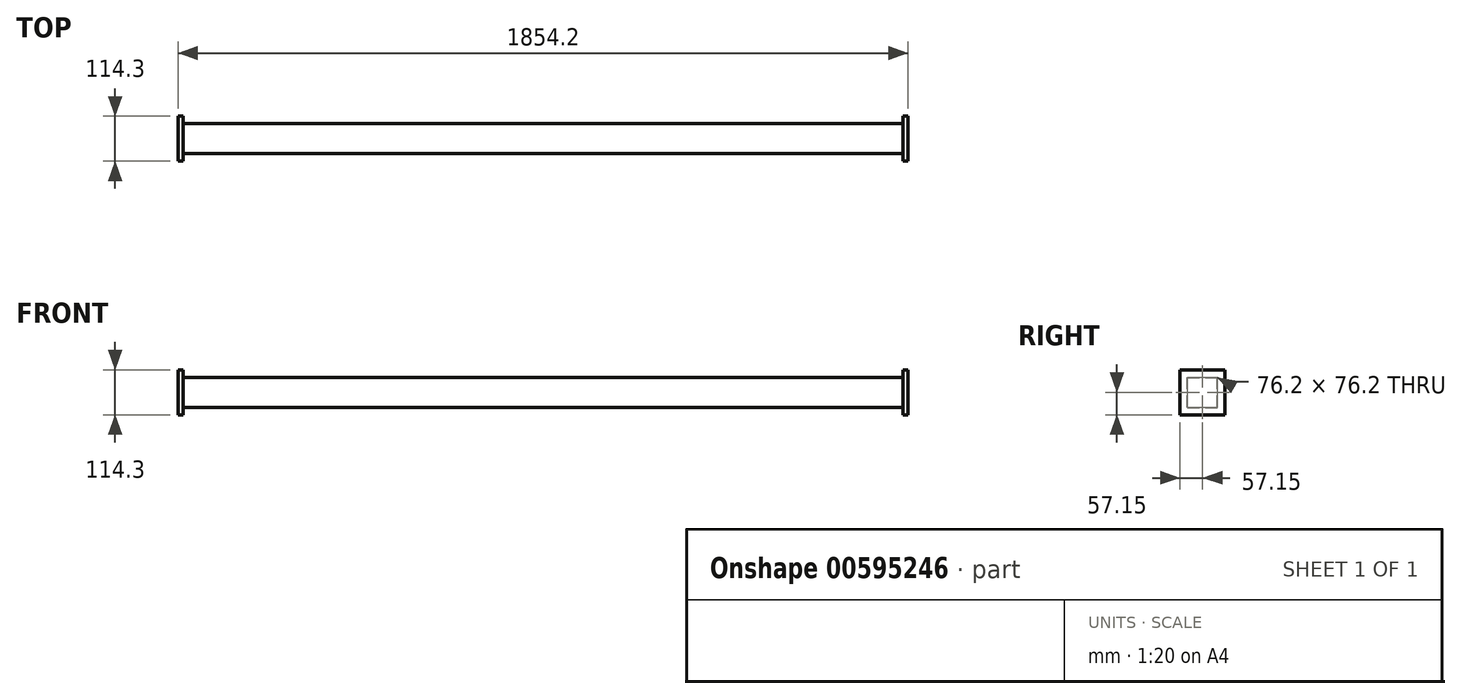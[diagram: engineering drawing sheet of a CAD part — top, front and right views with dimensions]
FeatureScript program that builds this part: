
annotation { "Feature Type Name" : "Feature", "Feature Type Description" : "" }
export const myFeature = defineFeature(function(context is Context, id is Id, definition is map)
    precondition{}
    {
        {
            var Q0;
            Q0=qCreatedBy(makeId("Right.planeOp"),FACE);
            var sketch = newSketch(context, id + "F0", { "sketchPlane" : qUnion([Q0])});
            skLineSegment(sketch, "E0.bottom", {"start": v(4231.19, -3979.39) * mm, "end": v(4078.79, -3979.39) * mm});
            skLineSegment(sketch, "E0.top", {"start": v(4231.19, -3826.99) * mm, "end": v(4078.79, -3826.99) * mm});
            skLineSegment(sketch, "E0.left", {"start": v(4231.19, -3979.39) * mm, "end": v(4231.19, -3826.99) * mm});
            skLineSegment(sketch, "E0.right", {"start": v(4078.79, -3979.39) * mm, "end": v(4078.79, -3826.99) * mm});
            skPoint(sketch, "E0.middle", {"position": v(4154.99, -3903.19) * mm});
            skSolve(sketch);
        }
        {
            var Q0;
            Q0=makeQuery(id+"F0.imprint","IMPRINT",FACE,{"disambiguationData":[TD([[makeQuery(id+"F0.imprint","IMPRINT",EDGE,{"derivedFrom":sQuery(id+"F0.wireOp",EDGE,"E0.bottom")}),-1.0]])]});
            extrude(context, id + "F1", {"entities" : qUnion([Q0]), "depth" : 12.7 * mm, "offsetDistance" : 25.4 * mm});
        }
        {
            var Q0;
            Q0=makeQuery(id+"F1.opExtrude","SWEPT_BODY",BODY,{"disambiguationData":[OSD([sQuery(id+"F0.wireOp",EDGE,"E0.bottom"),sQuery(id+"F0.wireOp",EDGE,"E0.top"),sQuery(id+"F0.wireOp",EDGE,"E0.left"),sQuery(id+"F0.wireOp",EDGE,"E0.right")])]});
            transform(context, id + "F2", {"entities" : qUnion([Q0]), "transformType" : TransformType.TRANSLATION_3D, "dx" : 706.12 * mm, "dy" : -1079.5 * mm, "dz" : 1186.18 * mm, "makeCopy" : false});
        }
        {
            var Q0;
            Q0=makeQuery(id+"F1.opExtrude","SWEPT_BODY",BODY,{"disambiguationData":[OSD([sQuery(id+"F0.wireOp",EDGE,"E0.bottom"),sQuery(id+"F0.wireOp",EDGE,"E0.top"),sQuery(id+"F0.wireOp",EDGE,"E0.left"),sQuery(id+"F0.wireOp",EDGE,"E0.right")])]});
            deleteBodies(context, id + "F3", {"entities" : qUnion([Q0])});
        }
        {
            var Q0;
            Q0=qCreatedBy(makeId("Front.planeOp"),FACE);
            var sketch = newSketch(context, id + "F4", { "sketchPlane" : qUnion([Q0])});
            skLineSegment(sketch, "E1.bottom", {"start": v(914.4, -38.1) * mm, "end": v(-914.4, -38.1) * mm});
            skLineSegment(sketch, "E1.top", {"start": v(914.4, 38.1) * mm, "end": v(-914.4, 38.1) * mm});
            skLineSegment(sketch, "E1.left", {"start": v(914.4, -38.1) * mm, "end": v(914.4, 38.1) * mm});
            skLineSegment(sketch, "E1.right", {"start": v(-914.4, -38.1) * mm, "end": v(-914.4, 38.1) * mm});
            skPoint(sketch, "E1.middle", {"position": v(0, 0) * mm});
            skSolve(sketch);
        }
        {
            var Q0;
            Q0=makeQuery(id+"F4.imprint","IMPRINT",FACE,{"disambiguationData":[TD([[makeQuery(id+"F4.imprint","IMPRINT",EDGE,{"derivedFrom":sQuery(id+"F4.wireOp",EDGE,"E1.bottom")}),-1.0]])]});
            extrude(context, id + "F5", {"entities" : qUnion([Q0]), "depth" : 76.2 * mm, "offsetDistance" : 25.4 * mm});
        }
        {
            var Q0;
            Q0=makeQuery(id+"F5.opExtrude","SWEPT_FACE",FACE,{"disambiguationData":[OSD([sQuery(id+"F4.wireOp",EDGE,"E1.left")])]});
            var sketch = newSketch(context, id + "F6", { "sketchPlane" : qUnion([Q0])});
            skLineSegment(sketch, "E2.bottom", {"start": v(19.05, -57.15) * mm, "end": v(-95.25, -57.15) * mm});
            skLineSegment(sketch, "E2.top", {"start": v(19.05, 57.15) * mm, "end": v(-95.25, 57.15) * mm});
            skLineSegment(sketch, "E2.left", {"start": v(19.05, -57.15) * mm, "end": v(19.05, 57.15) * mm});
            skLineSegment(sketch, "E2.right", {"start": v(-95.25, -57.15) * mm, "end": v(-95.25, 57.15) * mm});
            skPoint(sketch, "E2.middle", {"position": v(-38.1, 0) * mm});
            skPoint(sketch, "E2.middle.positionSnap0", {"position": v(-38.1, 38.1) * mm});
            skPoint(sketch, "E2.centerSnap0", {"position": v(-38.1, 38.1) * mm});
            skSolve(sketch);
        }
        {
            var Q0;
            {var subQ0=sQuery(id+"F4.wireOp",EDGE,"E1.left");Q0=makeQuery(id+"F6.imprint","IMPRINT",FACE,{"disambiguationData":[TD([[makeQuery(id+"F6.imprint","IMPRINT",EDGE,{"derivedFrom":makeQuery(id+"F5.opExtrude","CAP_EDGE",EDGE,{"disambiguationData":[OSD([subQ0])],"isStart":true})}),1.0]])]});}
            var Q1;
            Q1=makeQuery(id+"F6.imprint","IMPRINT",FACE,{"disambiguationData":[TD([[makeQuery(id+"F6.imprint","IMPRINT",EDGE,{"derivedFrom":sQuery(id+"F6.wireOp",EDGE,"E2.bottom")}),-1.0]])]});
            extrude(context, id + "F7", {"entities" : qUnion([Q0, Q1]), "operationType" : NewBodyOperationType.ADD, "depth" : 12.7 * mm, "offsetDistance" : 25.4 * mm});
        }
        {
            var Q0;
            Q0=makeQuery(id+"F5.opExtrude","SWEPT_FACE",FACE,{"disambiguationData":[OSD([sQuery(id+"F4.wireOp",EDGE,"E1.right")])]});
            var sketch = newSketch(context, id + "F8", { "sketchPlane" : qUnion([Q0])});
            skLineSegment(sketch, "E3.bottom", {"start": v(95.25, -57.15) * mm, "end": v(-19.05, -57.15) * mm});
            skLineSegment(sketch, "E3.top", {"start": v(95.25, 57.15) * mm, "end": v(-19.05, 57.15) * mm});
            skLineSegment(sketch, "E3.left", {"start": v(95.25, -57.15) * mm, "end": v(95.25, 57.15) * mm});
            skLineSegment(sketch, "E3.right", {"start": v(-19.05, -57.15) * mm, "end": v(-19.05, 57.15) * mm});
            skPoint(sketch, "E3.middle", {"position": v(38.1, 0) * mm});
            skPoint(sketch, "E3.middle.positionSnap0", {"position": v(38.1, 38.1) * mm});
            skPoint(sketch, "E3.centerSnap0", {"position": v(38.1, 38.1) * mm});
            skSolve(sketch);
        }
        {
            var Q0;
            Q0 = qSketchRegion(id + "F8", true);
            extrude(context, id + "F9", {"entities" : qUnion([Q0]), "operationType" : NewBodyOperationType.ADD, "depth" : 12.7 * mm, "offsetDistance" : 25.4 * mm});
        }
    });
